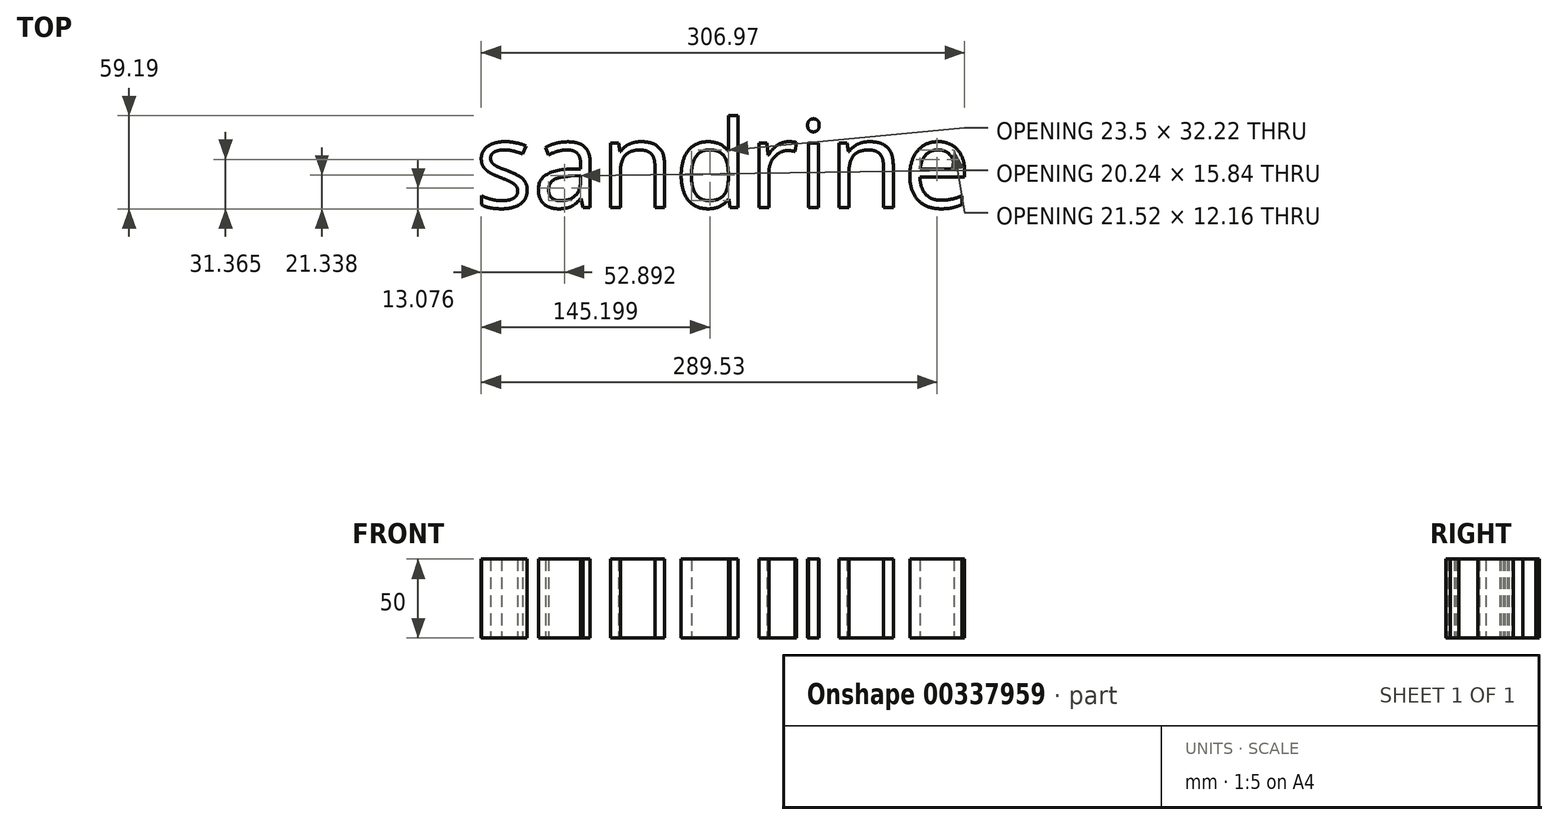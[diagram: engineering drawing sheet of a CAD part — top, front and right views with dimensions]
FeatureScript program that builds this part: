
annotation { "Feature Type Name" : "Feature", "Feature Type Description" : "" }
export const myFeature = defineFeature(function(context is Context, id is Id, definition is map)
    precondition{}
    {
        {
            var Q0;
            Q0=qCreatedBy(makeId("Top.planeOp"),FACE);
            var sketch = newSketch(context, id + "F0", { "sketchPlane" : qUnion([Q0])});
            skText(sketch, "E0", { "text": "sandrine\n", "fontName": "OpenSans-Regular.ttf"});
            const initialGuessF0  = {"E0": [-0.31592, -0.05537, 1, 0, 0.05537]};
            skSetInitialGuess(sketch, initialGuessF0);
            skSolve(sketch);
        }
        {
            var Q0;
            Q0 = qSketchRegion(id + "F0", true);
            extrude(context, id + "F1", {"entities" : qUnion([Q0]), "depth" : 50 * mm});
        }
    });
